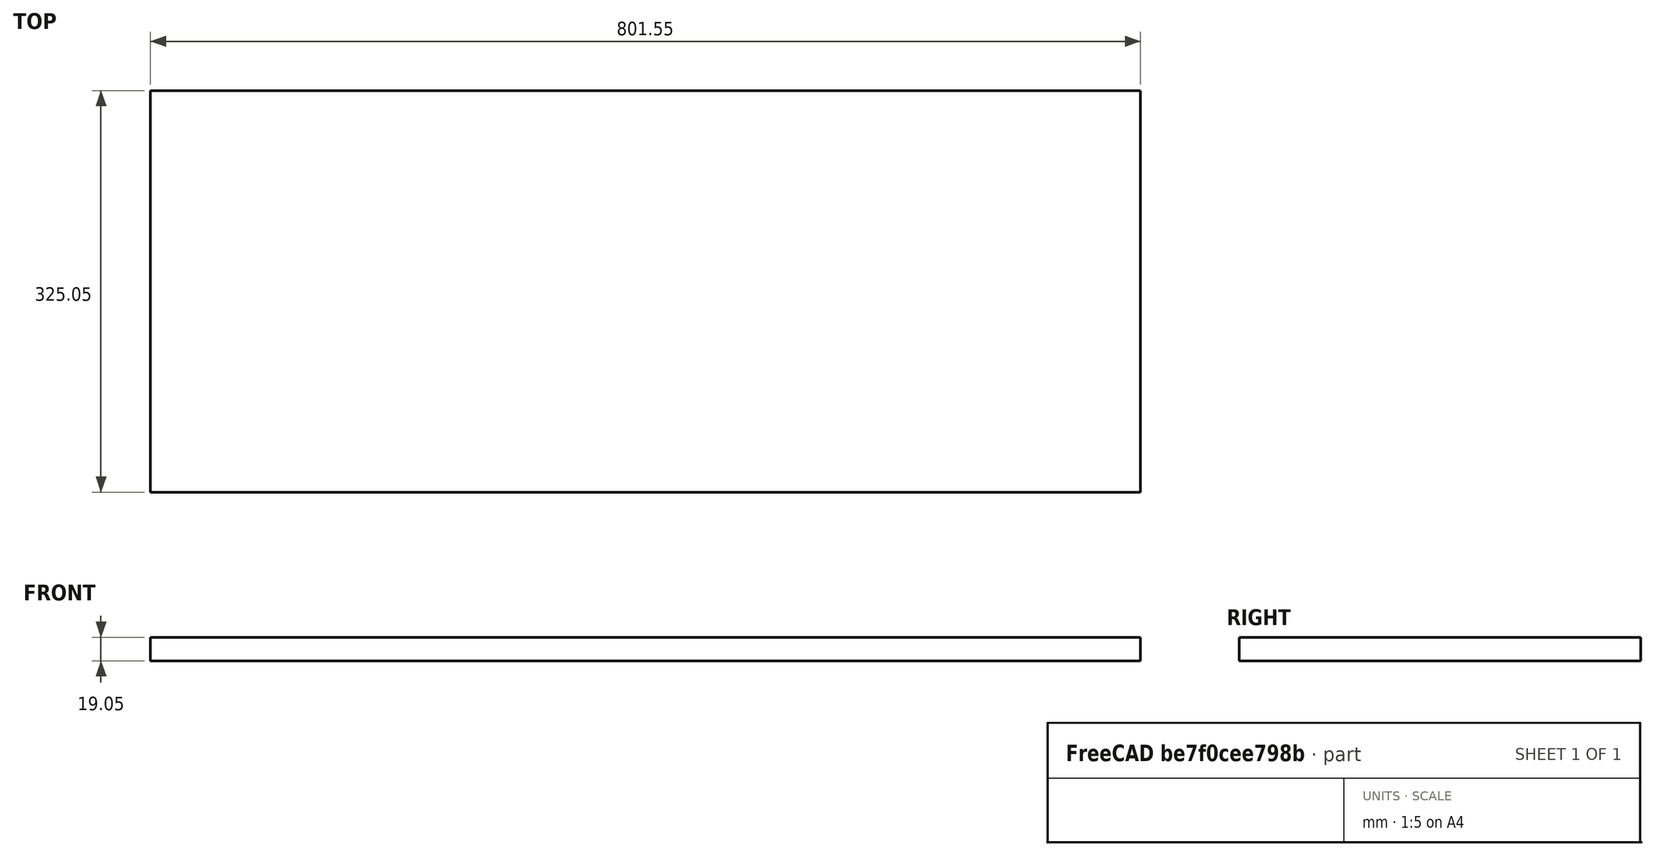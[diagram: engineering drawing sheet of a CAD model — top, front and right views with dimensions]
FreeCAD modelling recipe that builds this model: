
FCSTD DOCUMENT  (FreeCAD 0.20R29177 (Git))
Label: topRightPlywood
License: All rights reserved
LicenseURL: http://en.wikipedia.org/wiki/All_rights_reserved
objects: Sketcher::SketchObject×1, PartDesign::Pad×1, PartDesign::Body×1
note: 4 computed .brp shape members not serialized (recipe doc carries the construction recipe); baked Part::Feature solids carry a one-line shape summary decoded from their .brp

FEATURE [Sketcher::SketchObject] Sketch
  FullyConstrained = true
  MapMode = 5
  Support = -> [XY_Plane]
  expr: Constraints[10] = 650.1 / 2
  sketch-geometry (4):
    g0: LineSegment StartX=0 StartY=0 StartZ=0 EndX=801.55 EndY=0 EndZ=0
    g1: LineSegment StartX=801.55 StartY=0 StartZ=0 EndX=801.55 EndY=325.05 EndZ=0
    g2: LineSegment StartX=801.55 StartY=325.05 StartZ=0 EndX=0 EndY=325.05 EndZ=0
    g3: LineSegment StartX=0 StartY=325.05 StartZ=0 EndX=0 EndY=0 EndZ=0
  constraints (11):
    c: Coincident(g0,g1)
    c: Coincident(g1,g2)
    c: Coincident(g2,g3)
    c: Coincident(g3,g0)
    c: Horizontal(g0)
    c: Horizontal(g2)
    c: Vertical(g1)
    c: Vertical(g3)
    c: Coincident(g0,g-1)
    c: DistanceX(g0,g0) = 801.55
    c: DistanceY(g3,g3) = 325.05
FEATURE [PartDesign::Pad] Pad
  Direction = (0,0,1)
  Length = 19.05
  Length2 = 10
  Profile = -> Sketch
  ReferenceAxis = -> Sketch [N_Axis]
  Type = 0
  expr: Length = 3 / 4 * 25.4
FEATURE [PartDesign::Body] Body
  Group = -> [Sketch,Pad]
  Origin = -> Origin
  Tip = -> Pad
